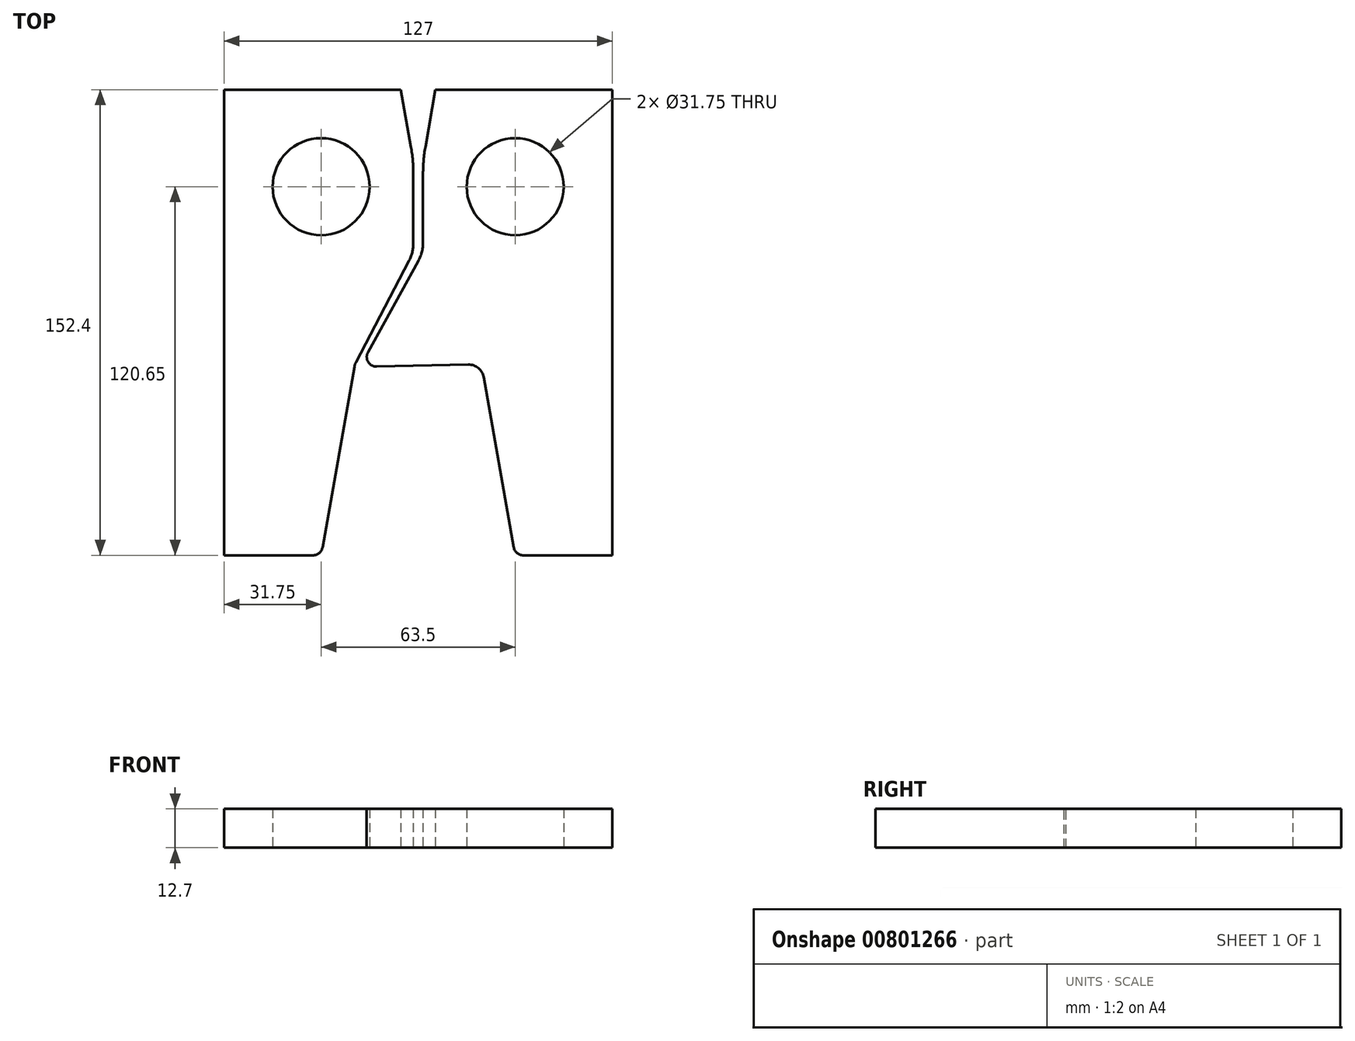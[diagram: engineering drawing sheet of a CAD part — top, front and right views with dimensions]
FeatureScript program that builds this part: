
annotation { "Feature Type Name" : "Feature", "Feature Type Description" : "" }
export const myFeature = defineFeature(function(context is Context, id is Id, definition is map)
    precondition{}
    {
        {
            var Q0;
            Q0=qCreatedBy(makeId("Top.planeOp"),FACE);
            var sketch = newSketch(context, id + "F0", { "sketchPlane" : qUnion([Q0])});
            skLineSegment(sketch, "E0.bottom", {"start": v(63.5, -76.2) * mm, "end": v(-63.5, -76.2) * mm});
            skLineSegment(sketch, "E0.top", {"start": v(63.5, 76.2) * mm, "end": v(-63.5, 76.2) * mm});
            skLineSegment(sketch, "E0.left", {"start": v(63.5, -76.2) * mm, "end": v(63.5, 76.2) * mm});
            skLineSegment(sketch, "E0.right", {"start": v(-63.5, -76.2) * mm, "end": v(-63.5, 76.2) * mm});
            skPoint(sketch, "E0.middle", {"position": v(0, 0) * mm});
            skPoint(sketch, "E1.middle", {"position": v(0, -76.2) * mm});
            skLineSegment(sketch, "E2", {"start": v(-31.75, -76.2) * mm, "end": v(-20.72, -13.66) * mm});
            skLineSegment(sketch, "E3.MirrorCS", {"start": v(31.75, -76.2) * mm, "end": v(20.72, -13.66) * mm});
            skLineSegment(sketch, "E4", {"start": v(20.72, -13.66) * mm, "end": v(-19.1, -14.55) * mm});
            skLineSegment(sketch, "E5", {"start": v(-5.65, 76.2) * mm, "end": v(-1.59, 53.15) * mm});
            skLineSegment(sketch, "E6.MirrorCS", {"start": v(5.65, 76.2) * mm, "end": v(1.59, 53.15) * mm});
            skLineSegment(sketch, "E7", {"start": v(1.59, 53.15) * mm, "end": v(1.59, 22.9) * mm});
            skLineSegment(sketch, "E8", {"start": v(1.59, 22.9) * mm, "end": v(-19.1, -14.55) * mm});
            skLineSegment(sketch, "E9.MirrorCS", {"start": v(-1.59, 53.15) * mm, "end": v(-1.59, 22.9) * mm});
            skLineSegment(sketch, "E10", {"start": v(-20.72, -13.66) * mm, "end": v(-1.59, 22.9) * mm});
            skCircle(sketch, "E11", {"center": v(-31.75, 44.45) * mm, "radius": 15.88 * mm});
            skCircle(sketch, "E12.MirrorC", {"center": v(31.75, 44.45) * mm, "radius": 15.88 * mm});
            skSolve(sketch);
        }
        {
            var Q0;
            {var subQ1=sQuery(id+"F0.wireOp",EDGE,"E0.left");Q0=makeQuery(id+"F0.imprint","IMPRINT",FACE,{"disambiguationData":[TD([[makeQuery(id+"F0.imprint","IMPRINT",EDGE,{"derivedFrom":subQ1}),1.0]])]});}
            var Q1;
            {var subQ1=sQuery(id+"F0.wireOp",EDGE,"E0.right");Q1=makeQuery(id+"F0.imprint","IMPRINT",FACE,{"disambiguationData":[TD([[makeQuery(id+"F0.imprint","IMPRINT",EDGE,{"derivedFrom":subQ1}),-1.0]])]});}
            extrude(context, id + "F1", {"entities" : qUnion([Q0, Q1]), "flatOperationType" : FlatOperationType.REMOVE, "depth" : 12.7 * mm, "offsetDistance" : 25.4 * mm, "domain" : OperationDomain.MODEL});
        }
        {
            var Q0;
            Q0=makeQuery(id+"F1.opExtrude","SWEPT_EDGE",EDGE,{"disambiguationData":[OSD([sQuery(id+"F0.wireOp",EDGE,"E7"),sQuery(id+"F0.wireOp",EDGE,"E8")])]});
            var Q1;
            Q1=makeQuery(id+"F1.opExtrude","SWEPT_EDGE",EDGE,{"disambiguationData":[OSD([sQuery(id+"F0.wireOp",EDGE,"E9.MirrorCS"),sQuery(id+"F0.wireOp",EDGE,"E10")])]});
            fillet(context, id + "F2", {"entities" : qUnion([Q0, Q1]), "radius" : 12.7 * mm, "tangentPropagation" : true, "allowEdgeOverflow" : false});
        }
        {
            var Q0;
            Q0=makeQuery(id+"F1.opExtrude","SWEPT_EDGE",EDGE,{"disambiguationData":[OSD([sQuery(id+"F0.wireOp",EDGE,"E6.MirrorCS"),sQuery(id+"F0.wireOp",EDGE,"E7")])]});
            var Q1;
            Q1=makeQuery(id+"F1.opExtrude","SWEPT_EDGE",EDGE,{"disambiguationData":[OSD([sQuery(id+"F0.wireOp",EDGE,"E5"),sQuery(id+"F0.wireOp",EDGE,"E9.MirrorCS")])]});
            fillet(context, id + "F3", {"entities" : qUnion([Q0, Q1]), "radius" : 50.8 * mm, "tangentPropagation" : true, "allowEdgeOverflow" : false});
        }
        {
            var Q0;
            Q0=makeQuery(id+"F1.opExtrude","SWEPT_EDGE",EDGE,{"disambiguationData":[OSD([sQuery(id+"F0.wireOp",EDGE,"E4"),sQuery(id+"F0.wireOp",EDGE,"E8")])]});
            fillet(context, id + "F4", {"entities" : qUnion([Q0]), "radius" : 3.17 * mm, "tangentPropagation" : true, "allowEdgeOverflow" : false});
        }
        {
            var Q0;
            Q0=makeQuery(id+"F1.opExtrude","SWEPT_EDGE",EDGE,{"disambiguationData":[OSD([sQuery(id+"F0.wireOp",EDGE,"E3.MirrorCS"),sQuery(id+"F0.wireOp",EDGE,"E4")])]});
            var Q1;
            Q1=makeQuery(id+"F1.opExtrude","SWEPT_EDGE",EDGE,{"disambiguationData":[OSD([sQuery(id+"F0.wireOp",EDGE,"E2"),sQuery(id+"F0.wireOp",EDGE,"E10")])]});
            fillet(context, id + "F5", {"entities" : qUnion([Q0, Q1]), "radius" : 5.08 * mm, "tangentPropagation" : true, "allowEdgeOverflow" : false});
        }
        {
            var Q0;
            Q0=makeQuery(id+"F1.opExtrude","SWEPT_EDGE",EDGE,{"disambiguationData":[OSD([sQuery(id+"F0.wireOp",EDGE,"E0.bottom"),sQuery(id+"F0.wireOp",EDGE,"E2")])]});
            var Q1;
            Q1=makeQuery(id+"F1.opExtrude","SWEPT_EDGE",EDGE,{"disambiguationData":[OSD([sQuery(id+"F0.wireOp",EDGE,"E0.bottom"),sQuery(id+"F0.wireOp",EDGE,"E3.MirrorCS")])]});
            fillet(context, id + "F6", {"entities" : qUnion([Q0, Q1]), "radius" : 3.17 * mm, "tangentPropagation" : true, "allowEdgeOverflow" : false});
        }
    });
